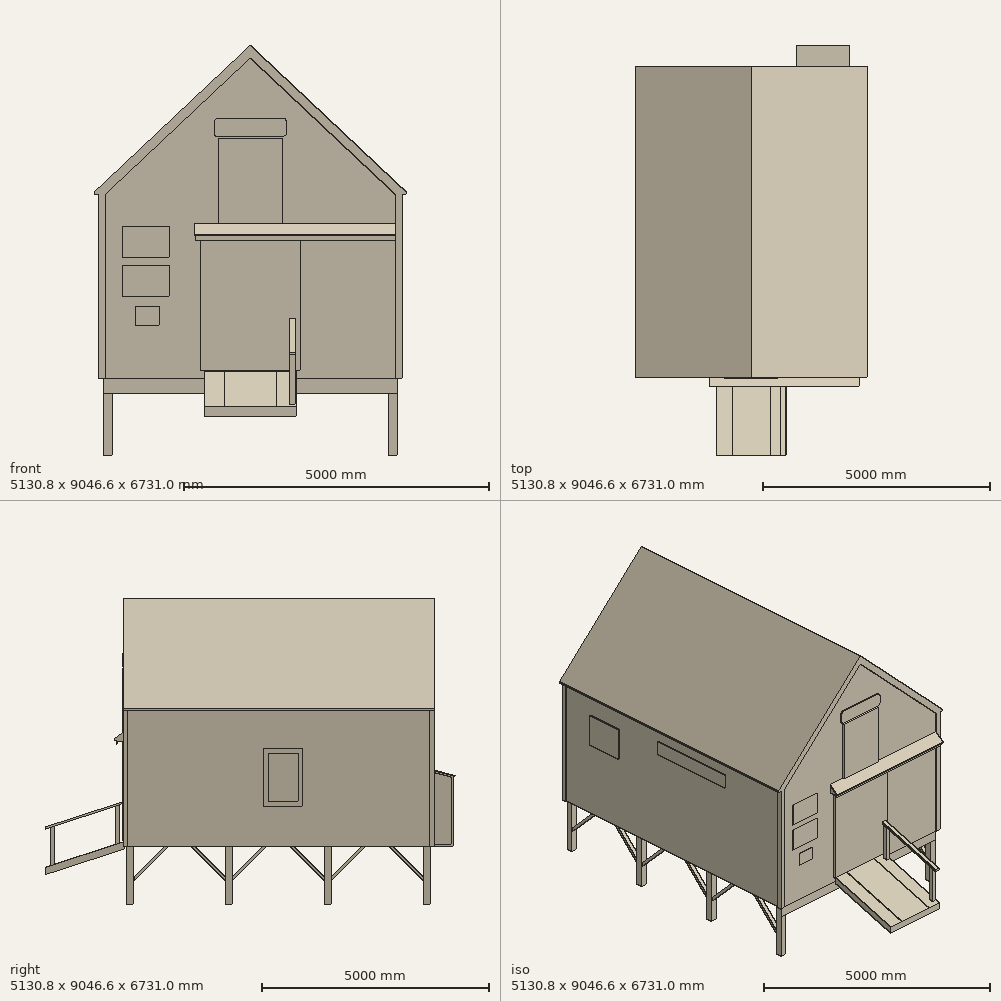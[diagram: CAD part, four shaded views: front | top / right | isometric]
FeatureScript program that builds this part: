
annotation { "Feature Type Name" : "Feature", "Feature Type Description" : "" }
export const myFeature = defineFeature(function(context is Context, id is Id, definition is map)
    precondition{}
    {
        {
            var Q0;
            Q0=qCreatedBy(makeId("Front.planeOp"),FACE);
            var sketch = newSketch(context, id + "F0", { "sketchPlane" : qUnion([Q0])});
            skLineSegment(sketch, "E0", {"start": v(0, 0) * mm, "end": v(0, 3048) * mm});
            skLineSegment(sketch, "E1", {"start": v(0, 3048) * mm, "end": v(2565.4, 5461) * mm});
            skLineSegment(sketch, "E2", {"start": v(2565.4, 5461) * mm, "end": v(5130.8, 3048) * mm});
            skLineSegment(sketch, "E3", {"start": v(5130.8, 3048) * mm, "end": v(5130.8, 0) * mm});
            skLineSegment(sketch, "E4", {"start": v(5130.8, 0) * mm, "end": v(0, 0) * mm});
            skLineSegment(sketch, "E5", {"start": v(2565.4, 5461) * mm, "end": v(2565.4, 0) * mm, "construction": true});
            skSolve(sketch);
        }
        {
            var Q0;
            Q0 = qSketchRegion(id + "F0", true);
            extrude(context, id + "F1", {"entities" : qUnion([Q0]), "oppositeDirection" : true, "depth" : 6858 * mm});
        }
        {
            var Q0;
            Q0=makeQuery(id+"F1.opExtrude","CAP_FACE",FACE,{"disambiguationData":[OSD([sQuery(id+"F0.wireOp",EDGE,"E0"),sQuery(id+"F0.wireOp",EDGE,"E1"),sQuery(id+"F0.wireOp",EDGE,"E2"),sQuery(id+"F0.wireOp",EDGE,"E3"),sQuery(id+"F0.wireOp",EDGE,"E4")])],"isStart":true});
            var sketch = newSketch(context, id + "F2", { "sketchPlane" : qUnion([Q0])});
            skLineSegment(sketch, "E6.bottom", {"start": v(0, 0) * mm, "end": v(76.2, 0) * mm});
            skLineSegment(sketch, "E6.top", {"start": v(0, 3009.9) * mm, "end": v(76.2, 3009.9) * mm});
            skLineSegment(sketch, "E6.left", {"start": v(0, 0) * mm, "end": v(0, 3009.9) * mm});
            skLineSegment(sketch, "E6.right", {"start": v(76.2, 0) * mm, "end": v(76.2, 3009.9) * mm});
            skLineSegment(sketch, "E7.bottom", {"start": v(5130.8, 0) * mm, "end": v(5054.6, 0) * mm});
            skLineSegment(sketch, "E7.top", {"start": v(5130.8, 3009.9) * mm, "end": v(5054.6, 3009.9) * mm});
            skLineSegment(sketch, "E7.left", {"start": v(5130.8, 0) * mm, "end": v(5130.8, 3009.9) * mm});
            skLineSegment(sketch, "E7.right", {"start": v(5054.6, 0) * mm, "end": v(5054.6, 3009.9) * mm});
            skSolve(sketch);
        }
        {
            var Q0;
            Q0 = qSketchRegion(id + "F2", true);
            extrude(context, id + "F3", {"entities" : qUnion([Q0]), "operationType" : NewBodyOperationType.REMOVE, "endBound" : BoundingType.THROUGH_ALL, "oppositeDirection" : true, "depth" : 25.4 * mm});
        }
        {
            var Q0;
            Q0=makeQuery(id+"F1.opExtrude","CAP_FACE",FACE,{"disambiguationData":[OSD([sQuery(id+"F0.wireOp",EDGE,"E0"),sQuery(id+"F0.wireOp",EDGE,"E1"),sQuery(id+"F0.wireOp",EDGE,"E2"),sQuery(id+"F0.wireOp",EDGE,"E3"),sQuery(id+"F0.wireOp",EDGE,"E4")])],"isStart":true});
            var sketch = newSketch(context, id + "F4", { "sketchPlane" : qUnion([Q0])});
            skLineSegment(sketch, "E8", {"start": v(177.8, 0) * mm, "end": v(177.8, 3006.02) * mm});
            skLineSegment(sketch, "E9", {"start": v(177.8, 3006.02) * mm, "end": v(2565.4, 5251.78) * mm});
            skLineSegment(sketch, "E10", {"start": v(2565.4, 5251.78) * mm, "end": v(4953, 3006.02) * mm});
            skLineSegment(sketch, "E11", {"start": v(4953, 3006.02) * mm, "end": v(4953, 0) * mm});
            skSolve(sketch);
        }
        {
            var Q0;
            {var subQ1=sQuery(id+"F4.wireOp",EDGE,"E8");Q0=makeQuery(id+"F4.imprint","IMPRINT",FACE,{"disambiguationData":[TD([[makeQuery(id+"F4.imprint","IMPRINT",EDGE,{"derivedFrom":subQ1}),-1.0]])]});}
            extrude(context, id + "F5", {"entities" : qUnion([Q0]), "operationType" : NewBodyOperationType.REMOVE, "oppositeDirection" : true, "depth" : 25.4 * mm});
        }
        {
            var Q0;
            Q0=makeQuery(id+"F1.opExtrude","CAP_FACE",FACE,{"disambiguationData":[OSD([sQuery(id+"F0.wireOp",EDGE,"E0"),sQuery(id+"F0.wireOp",EDGE,"E1"),sQuery(id+"F0.wireOp",EDGE,"E2"),sQuery(id+"F0.wireOp",EDGE,"E3"),sQuery(id+"F0.wireOp",EDGE,"E4")])],"isStart":false});
            var sketch = newSketch(context, id + "F6", { "sketchPlane" : qUnion([Q0])});
            skLineSegment(sketch, "E12.0.0", {"start": v(-4953, 0) * mm, "end": v(-4953, 3006.02) * mm});
            skLineSegment(sketch, "E12.0.1", {"start": v(-4953, 3006.02) * mm, "end": v(-2565.4, 5251.78) * mm});
            skLineSegment(sketch, "E12.0.2", {"start": v(-2565.4, 5251.78) * mm, "end": v(-177.8, 3006.02) * mm});
            skLineSegment(sketch, "E12.0.3", {"start": v(-177.8, 3006.02) * mm, "end": v(-177.8, 0) * mm});
            skLineSegment(sketch, "E12.0.4", {"start": v(-177.8, 0) * mm, "end": v(-4953, 0) * mm});
            skSolve(sketch);
        }
        {
            var Q0;
            Q0 = qSketchRegion(id + "F6", true);
            extrude(context, id + "F7", {"entities" : qUnion([Q0]), "operationType" : NewBodyOperationType.REMOVE, "oppositeDirection" : true, "depth" : 25.4 * mm});
        }
        {
            var Q0;
            Q0=makeQuery(id+"F3.boolean.opBoolean","COPY",FACE,{"derivedFrom":makeQuery(id+"F3.opExtrude","SWEPT_FACE",FACE,{"disambiguationData":[OSD([sQuery(id+"F2.wireOp",EDGE,"E6.right")])]})});
            var sketch = newSketch(context, id + "F8", { "sketchPlane" : qUnion([Q0])});
            skLineSegment(sketch, "E13.bottom", {"start": v(-6858, 0) * mm, "end": v(-6756.4, 0) * mm});
            skLineSegment(sketch, "E13.top", {"start": v(-6858, 3009.9) * mm, "end": v(-6756.4, 3009.9) * mm});
            skLineSegment(sketch, "E13.left", {"start": v(-6858, 0) * mm, "end": v(-6858, 3009.9) * mm});
            skLineSegment(sketch, "E13.right", {"start": v(-6756.4, 0) * mm, "end": v(-6756.4, 3009.9) * mm});
            skLineSegment(sketch, "E14.bottom", {"start": v(0, 0) * mm, "end": v(-101.6, 0) * mm});
            skLineSegment(sketch, "E14.top", {"start": v(0, 3009.9) * mm, "end": v(-101.6, 3009.9) * mm});
            skLineSegment(sketch, "E14.left", {"start": v(0, 0) * mm, "end": v(0, 3009.9) * mm});
            skLineSegment(sketch, "E14.right", {"start": v(-101.6, 0) * mm, "end": v(-101.6, 3009.9) * mm});
            skSolve(sketch);
        }
        {
            var Q0;
            {var subQ0=sQuery(id+"F8.wireOp",EDGE,"E13.right");Q0=makeQuery(id+"F8.imprint","IMPRINT",FACE,{"disambiguationData":[TD([[makeQuery(id+"F8.imprint","IMPRINT",EDGE,{"derivedFrom":subQ0}),-1.0]])]});}
            extrude(context, id + "F9", {"entities" : qUnion([Q0]), "operationType" : NewBodyOperationType.REMOVE, "oppositeDirection" : true, "depth" : 25.4 * mm});
        }
        {
            var Q0;
            Q0=makeQuery(id+"F3.boolean.opBoolean","COPY",FACE,{"derivedFrom":makeQuery(id+"F3.opExtrude","SWEPT_FACE",FACE,{"disambiguationData":[OSD([sQuery(id+"F2.wireOp",EDGE,"E7.right")])]})});
            var sketch = newSketch(context, id + "F10", { "sketchPlane" : qUnion([Q0])});
            skLineSegment(sketch, "E15.0.0", {"start": v(6756.4, 0) * mm, "end": v(101.6, 0) * mm});
            skLineSegment(sketch, "E15.0.1", {"start": v(101.6, 0) * mm, "end": v(101.6, 3009.9) * mm});
            skLineSegment(sketch, "E15.0.2", {"start": v(101.6, 3009.9) * mm, "end": v(6756.4, 3009.9) * mm});
            skLineSegment(sketch, "E15.0.3", {"start": v(6756.4, 3009.9) * mm, "end": v(6756.4, 0) * mm});
            skSolve(sketch);
        }
        {
            var Q0;
            Q0 = qSketchRegion(id + "F10", true);
            extrude(context, id + "F11", {"entities" : qUnion([Q0]), "operationType" : NewBodyOperationType.REMOVE, "oppositeDirection" : true, "depth" : 25.4 * mm});
        }
        {
            var Q0;
            Q0=makeQuery(id+"F1.opExtrude","SWEPT_FACE",FACE,{"disambiguationData":[OSD([sQuery(id+"F0.wireOp",EDGE,"E4")])]});
            var sketch = newSketch(context, id + "F12", { "sketchPlane" : qUnion([Q0])});
            skLineSegment(sketch, "E16.bottom", {"start": v(152.4, -76.2) * mm, "end": v(304.8, -76.2) * mm});
            skLineSegment(sketch, "E16.top", {"start": v(152.4, -228.6) * mm, "end": v(304.8, -228.6) * mm});
            skLineSegment(sketch, "E16.left", {"start": v(152.4, -76.2) * mm, "end": v(152.4, -228.6) * mm});
            skLineSegment(sketch, "E16.right", {"start": v(304.8, -76.2) * mm, "end": v(304.8, -228.6) * mm});
            skLineSegment(sketch, "E17.bottom", {"start": v(152.4, -2260.6) * mm, "end": v(304.8, -2260.6) * mm});
            skLineSegment(sketch, "E17.top", {"start": v(152.4, -2413) * mm, "end": v(304.8, -2413) * mm});
            skLineSegment(sketch, "E17.left", {"start": v(152.4, -2260.6) * mm, "end": v(152.4, -2413) * mm});
            skLineSegment(sketch, "E17.right", {"start": v(304.8, -2260.6) * mm, "end": v(304.8, -2413) * mm});
            skLineSegment(sketch, "E18.bottom", {"start": v(152.4, -4445) * mm, "end": v(304.8, -4445) * mm});
            skLineSegment(sketch, "E18.top", {"start": v(152.4, -4597.4) * mm, "end": v(304.8, -4597.4) * mm});
            skLineSegment(sketch, "E18.left", {"start": v(152.4, -4445) * mm, "end": v(152.4, -4597.4) * mm});
            skLineSegment(sketch, "E18.right", {"start": v(304.8, -4445) * mm, "end": v(304.8, -4597.4) * mm});
            skLineSegment(sketch, "E19.bottom", {"start": v(152.4, -6629.4) * mm, "end": v(304.8, -6629.4) * mm});
            skLineSegment(sketch, "E19.top", {"start": v(152.4, -6781.8) * mm, "end": v(304.8, -6781.8) * mm});
            skLineSegment(sketch, "E19.left", {"start": v(152.4, -6629.4) * mm, "end": v(152.4, -6781.8) * mm});
            skLineSegment(sketch, "E19.right", {"start": v(304.8, -6629.4) * mm, "end": v(304.8, -6781.8) * mm});
            skLineSegment(sketch, "E20.bottom", {"start": v(4826, -6629.4) * mm, "end": v(4978.4, -6629.4) * mm});
            skLineSegment(sketch, "E20.top", {"start": v(4826, -6781.8) * mm, "end": v(4978.4, -6781.8) * mm});
            skLineSegment(sketch, "E20.left", {"start": v(4826, -6629.4) * mm, "end": v(4826, -6781.8) * mm});
            skLineSegment(sketch, "E20.right", {"start": v(4978.4, -6629.4) * mm, "end": v(4978.4, -6781.8) * mm});
            skLineSegment(sketch, "E21.bottom", {"start": v(4826, -4445) * mm, "end": v(4978.4, -4445) * mm});
            skLineSegment(sketch, "E21.top", {"start": v(4826, -4597.4) * mm, "end": v(4978.4, -4597.4) * mm});
            skLineSegment(sketch, "E21.left", {"start": v(4826, -4445) * mm, "end": v(4826, -4597.4) * mm});
            skLineSegment(sketch, "E21.right", {"start": v(4978.4, -4445) * mm, "end": v(4978.4, -4597.4) * mm});
            skLineSegment(sketch, "E22.bottom", {"start": v(4826, -2260.6) * mm, "end": v(4978.4, -2260.6) * mm});
            skLineSegment(sketch, "E22.top", {"start": v(4826, -2413) * mm, "end": v(4978.4, -2413) * mm});
            skLineSegment(sketch, "E22.left", {"start": v(4826, -2260.6) * mm, "end": v(4826, -2413) * mm});
            skLineSegment(sketch, "E22.right", {"start": v(4978.4, -2260.6) * mm, "end": v(4978.4, -2413) * mm});
            skLineSegment(sketch, "E23.bottom", {"start": v(4826, -76.2) * mm, "end": v(4978.4, -76.2) * mm});
            skLineSegment(sketch, "E23.top", {"start": v(4826, -228.6) * mm, "end": v(4978.4, -228.6) * mm});
            skLineSegment(sketch, "E23.left", {"start": v(4826, -76.2) * mm, "end": v(4826, -228.6) * mm});
            skLineSegment(sketch, "E23.right", {"start": v(4978.4, -76.2) * mm, "end": v(4978.4, -228.6) * mm});
            skLineSegment(sketch, "E24", {"start": v(304.8, -228.6) * mm, "end": v(304.8, -2260.6) * mm, "construction": true});
            skLineSegment(sketch, "E25", {"start": v(304.8, -2413) * mm, "end": v(304.8, -4445) * mm, "construction": true});
            skLineSegment(sketch, "E26", {"start": v(304.8, -6629.4) * mm, "end": v(304.8, -4597.4) * mm, "construction": true});
            skSolve(sketch);
        }
        {
            var Q0;
            Q0 = qSketchRegion(id + "F12", true);
            extrude(context, id + "F13", {"entities" : qUnion([Q0]), "operationType" : NewBodyOperationType.ADD, "depth" : 1270 * mm});
        }
        {
            var Q0;
            Q0=makeQuery(id+"F13.opExtrude","SWEPT_FACE",FACE,{"disambiguationData":[OSD([sQuery(id+"F12.wireOp",EDGE,"E22.right")])]});
            cPlane(context, id + "F14", {"entities" : qUnion([Q0]), "cplaneType" : CPlaneType.OFFSET, "offset" : 25.4 * mm, "oppositeDirection" : true, "width" : 152.4 * mm, "height" : 152.4 * mm});
        }
        {
            var Q0;
            Q0=qCreatedBy(id+"F14.planeOp",FACE);
            var sketch = newSketch(context, id + "F15", { "sketchPlane" : qUnion([Q0])});
            skLineSegment(sketch, "E27", {"start": v(1588.4, 0) * mm, "end": v(2260.6, -672.2) * mm});
            skLineSegment(sketch, "E28", {"start": v(2260.6, -672.2) * mm, "end": v(2260.6, -762) * mm});
            skLineSegment(sketch, "E29", {"start": v(2260.6, -762) * mm, "end": v(1498.6, 0) * mm});
            skLineSegment(sketch, "E30", {"start": v(1498.6, 0) * mm, "end": v(1588.4, 0) * mm});
            skLineSegment(sketch, "E31", {"start": v(2413, -672.2) * mm, "end": v(3085.2, 0) * mm});
            skLineSegment(sketch, "E32", {"start": v(3085.2, 0) * mm, "end": v(3175, 0) * mm});
            skLineSegment(sketch, "E33", {"start": v(3175, 0) * mm, "end": v(2413, -762) * mm});
            skLineSegment(sketch, "E34", {"start": v(2413, -762) * mm, "end": v(2413, -672.2) * mm});
            skLineSegment(sketch, "E35.1.0.0", {"start": v(4597.4, -672.2) * mm, "end": v(5269.6, 0) * mm});
            skLineSegment(sketch, "E35.1.0.1", {"start": v(4445, -762) * mm, "end": v(3683, 0) * mm});
            skLineSegment(sketch, "E35.1.0.2", {"start": v(5359.4, 0) * mm, "end": v(4597.4, -762) * mm});
            skLineSegment(sketch, "E35.1.0.3", {"start": v(3772.8, 0) * mm, "end": v(4445, -672.2) * mm});
            skLineSegment(sketch, "E35.1.0.4", {"start": v(4445, -672.2) * mm, "end": v(4445, -762) * mm});
            skLineSegment(sketch, "E35.1.0.5", {"start": v(5269.6, 0) * mm, "end": v(5359.4, 0) * mm});
            skLineSegment(sketch, "E35.1.0.6", {"start": v(3683, 0) * mm, "end": v(3772.8, 0) * mm});
            skLineSegment(sketch, "E35.1.0.7", {"start": v(4597.4, -762) * mm, "end": v(4597.4, -672.2) * mm});
            skLineSegment(sketch, "E35.2.0.1", {"start": v(6629.4, -762) * mm, "end": v(5867.4, 0) * mm});
            skLineSegment(sketch, "E35.2.0.3", {"start": v(5957.2, 0) * mm, "end": v(6629.4, -672.2) * mm});
            skLineSegment(sketch, "E35.2.0.4", {"start": v(6629.4, -672.2) * mm, "end": v(6629.4, -762) * mm});
            skLineSegment(sketch, "E35.2.0.6", {"start": v(5867.4, 0) * mm, "end": v(5957.2, 0) * mm});
            skLineSegment(sketch, "E35.direction1", {"start": v(2260.6, -762) * mm, "end": v(4445, -762) * mm, "construction": true});
            skLineSegment(sketch, "E36.1.0.2", {"start": v(254, -672.2) * mm, "end": v(926.2, 0) * mm});
            skLineSegment(sketch, "E36.1.0.3", {"start": v(1016, 0) * mm, "end": v(254, -762) * mm});
            skLineSegment(sketch, "E36.1.0.5", {"start": v(926.2, 0) * mm, "end": v(1016, 0) * mm});
            skLineSegment(sketch, "E36.1.0.6", {"start": v(254, -762) * mm, "end": v(254, -672.2) * mm});
            skLineSegment(sketch, "E36.direction1", {"start": v(2260.6, -762) * mm, "end": v(254, -762) * mm, "construction": true});
            skSolve(sketch);
        }
        {
            var Q0;
            Q0 = qSketchRegion(id + "F15", true);
            extrude(context, id + "F16", {"entities" : qUnion([Q0]), "operationType" : NewBodyOperationType.ADD, "oppositeDirection" : true, "depth" : 101.6 * mm});
        }
        {
            var Q0;
            Q0=makeQuery(id+"F1.opExtrude","SWEPT_FACE",FACE,{"disambiguationData":[OSD([sQuery(id+"F0.wireOp",EDGE,"E4")])]});
            var sketch = newSketch(context, id + "F17", { "sketchPlane" : qUnion([Q0])});
            skLineSegment(sketch, "E37.bottom", {"start": v(228.6, -76.2) * mm, "end": v(4927.6, -76.2) * mm});
            skLineSegment(sketch, "E37.top", {"start": v(228.6, -152.4) * mm, "end": v(4927.6, -152.4) * mm});
            skLineSegment(sketch, "E37.left", {"start": v(228.6, -76.2) * mm, "end": v(228.6, -152.4) * mm});
            skLineSegment(sketch, "E37.right", {"start": v(4927.6, -76.2) * mm, "end": v(4927.6, -152.4) * mm});
            skSolve(sketch);
        }
        {
            var Q0;
            Q0 = qSketchRegion(id + "F17", true);
            extrude(context, id + "F18", {"entities" : qUnion([Q0]), "operationType" : NewBodyOperationType.ADD, "depth" : 254 * mm});
        }
        {
            var Q0;
            Q0=makeQuery(id+"F13.opExtrude","SWEPT_FACE",FACE,{"disambiguationData":[OSD([sQuery(id+"F12.wireOp",EDGE,"E17.left")])]});
            cPlane(context, id + "F19", {"entities" : qUnion([Q0]), "cplaneType" : CPlaneType.OFFSET, "offset" : 25.4 * mm, "oppositeDirection" : true, "width" : 152.4 * mm, "height" : 152.4 * mm});
        }
        {
            var Q0;
            Q0=qCreatedBy(id+"F19.planeOp",FACE);
            var sketch = newSketch(context, id + "F20", { "sketchPlane" : qUnion([Q0])});
            skLineSegment(sketch, "E38.0.0", {"start": v(-1016, 0) * mm, "end": v(-216.67, -799.33) * mm});
            skLineSegment(sketch, "E38.0.1", {"start": v(-216.67, -799.33) * mm, "end": v(-228.85, -697.35) * mm});
            skLineSegment(sketch, "E38.0.2", {"start": v(-228.85, -697.35) * mm, "end": v(-926.2, 0) * mm});
            skLineSegment(sketch, "E38.0.3", {"start": v(-926.2, 0) * mm, "end": v(-1016, 0) * mm});
            skLineSegment(sketch, "E38.1.0", {"start": v(-1498.6, 0) * mm, "end": v(-1588.4, 0) * mm});
            skLineSegment(sketch, "E38.1.1", {"start": v(-1588.4, 0) * mm, "end": v(-2260.6, -672.2) * mm});
            skLineSegment(sketch, "E38.1.2", {"start": v(-2260.6, -672.2) * mm, "end": v(-2260.6, -762) * mm});
            skLineSegment(sketch, "E38.1.3", {"start": v(-2260.6, -762) * mm, "end": v(-1498.6, 0) * mm});
            skLineSegment(sketch, "E38.2.0", {"start": v(-2413, -762) * mm, "end": v(-2413, -672.2) * mm});
            skLineSegment(sketch, "E38.2.1", {"start": v(-2413, -672.2) * mm, "end": v(-3085.2, 0) * mm});
            skLineSegment(sketch, "E38.2.2", {"start": v(-3085.2, 0) * mm, "end": v(-3175, 0) * mm});
            skLineSegment(sketch, "E38.2.3", {"start": v(-3175, 0) * mm, "end": v(-2413, -762) * mm});
            skLineSegment(sketch, "E38.3.0", {"start": v(-4451.44, -678.64) * mm, "end": v(-4448.14, -765.14) * mm});
            skLineSegment(sketch, "E38.3.1", {"start": v(-4448.14, -765.14) * mm, "end": v(-3683, 0) * mm});
            skLineSegment(sketch, "E38.3.2", {"start": v(-3683, 0) * mm, "end": v(-3772.8, 0) * mm});
            skLineSegment(sketch, "E38.3.3", {"start": v(-3772.8, 0) * mm, "end": v(-4451.44, -678.64) * mm});
            skLineSegment(sketch, "E38.4.0", {"start": v(-5359.4, 0) * mm, "end": v(-4597.4, -762) * mm});
            skLineSegment(sketch, "E38.4.1", {"start": v(-4597.4, -762) * mm, "end": v(-4597.4, -672.2) * mm});
            skLineSegment(sketch, "E38.4.2", {"start": v(-4597.4, -672.2) * mm, "end": v(-5269.6, 0) * mm});
            skLineSegment(sketch, "E38.4.3", {"start": v(-5269.6, 0) * mm, "end": v(-5359.4, 0) * mm});
            skLineSegment(sketch, "E38.5.0", {"start": v(-6628.48, -671.28) * mm, "end": v(-6634.78, -767.38) * mm});
            skLineSegment(sketch, "E38.5.1", {"start": v(-6634.78, -767.38) * mm, "end": v(-5867.4, 0) * mm});
            skLineSegment(sketch, "E38.5.2", {"start": v(-5867.4, 0) * mm, "end": v(-5957.2, 0) * mm});
            skLineSegment(sketch, "E38.5.3", {"start": v(-5957.2, 0) * mm, "end": v(-6628.48, -671.28) * mm});
            skSolve(sketch);
        }
        {
            var Q0;
            Q0 = qSketchRegion(id + "F20", true);
            extrude(context, id + "F21", {"entities" : qUnion([Q0]), "operationType" : NewBodyOperationType.ADD, "oppositeDirection" : true, "depth" : 101.6 * mm});
        }
        {
            var Q0;
            Q0=makeQuery(id+"F5.boolean.opBoolean","COPY",FACE,{"derivedFrom":makeQuery(id+"F5.opExtrude","CAP_FACE",FACE,{"disambiguationData":[OSD([sQuery(id+"F0.wireOp",EDGE,"E4"),sQuery(id+"F4.wireOp",EDGE,"E8"),sQuery(id+"F4.wireOp",EDGE,"E9"),sQuery(id+"F4.wireOp",EDGE,"E10"),sQuery(id+"F4.wireOp",EDGE,"E11")])],"isStart":false})});
            var sketch = newSketch(context, id + "F22", { "sketchPlane" : qUnion([Q0])});
            skLineSegment(sketch, "E39.bottom", {"start": v(1739.9, 2286) * mm, "end": v(3390.9, 2286) * mm});
            skLineSegment(sketch, "E39.top", {"start": v(1739.9, 127) * mm, "end": v(3390.9, 127) * mm});
            skLineSegment(sketch, "E39.left", {"start": v(1739.9, 2286) * mm, "end": v(1739.9, 127) * mm});
            skLineSegment(sketch, "E39.right", {"start": v(3390.9, 2286) * mm, "end": v(3390.9, 127) * mm});
            skLineSegment(sketch, "E40", {"start": v(2565.4, 5251.78) * mm, "end": v(2565.4, 2286) * mm, "construction": true});
            skLineSegment(sketch, "E41.bottom", {"start": v(2032, 3937) * mm, "end": v(3098.8, 3937) * mm});
            skLineSegment(sketch, "E41.top", {"start": v(2032, 2540) * mm, "end": v(3098.8, 2540) * mm});
            skLineSegment(sketch, "E41.left", {"start": v(2032, 3937) * mm, "end": v(2032, 2540) * mm});
            skLineSegment(sketch, "E41.right", {"start": v(3098.8, 3937) * mm, "end": v(3098.8, 2540) * mm});
            skSolve(sketch);
        }
        {
            var Q0;
            Q0 = qSketchRegion(id + "F22", true);
            extrude(context, id + "F23", {"entities" : qUnion([Q0]), "operationType" : NewBodyOperationType.ADD, "depth" : 50.8 * mm});
        }
        {
            var Q0;
            Q0=makeQuery(id+"F23.opExtrude","SWEPT_FACE",FACE,{"disambiguationData":[OSD([sQuery(id+"F22.wireOp",EDGE,"E39.left")])]});
            cPlane(context, id + "F24", {"entities" : qUnion([Q0]), "cplaneType" : CPlaneType.OFFSET, "offset" : 101.6 * mm, "width" : 152.4 * mm, "height" : 152.4 * mm});
        }
        {
            var Q0;
            Q0=qCreatedBy(id+"F24.planeOp",FACE);
            var sketch = newSketch(context, id + "F25", { "sketchPlane" : qUnion([Q0])});
            skLineSegment(sketch, "E42", {"start": v(-25.4, 2540) * mm, "end": v(203.2, 2362.2) * mm});
            skLineSegment(sketch, "E43", {"start": v(203.2, 2362.2) * mm, "end": v(203.2, 2336.8) * mm});
            skLineSegment(sketch, "E44", {"start": v(203.2, 2336.8) * mm, "end": v(152.4, 2336.8) * mm});
            skLineSegment(sketch, "E45", {"start": v(152.4, 2336.8) * mm, "end": v(152.4, 2260.6) * mm});
            skLineSegment(sketch, "E46", {"start": v(152.4, 2260.6) * mm, "end": v(127, 2260.6) * mm});
            skLineSegment(sketch, "E47", {"start": v(127, 2260.6) * mm, "end": v(127, 2311.4) * mm});
            skLineSegment(sketch, "E48", {"start": v(127, 2311.4) * mm, "end": v(-25.4, 2311.4) * mm});
            skLineSegment(sketch, "E49", {"start": v(-25.4, 2540) * mm, "end": v(-25.4, 2311.4) * mm});
            skSolve(sketch);
        }
        {
            var Q0;
            Q0 = qSketchRegion(id + "F25", true);
            var Q1;
            Q1=makeQuery(id+"F5.boolean.opBoolean","COPY",FACE,{"derivedFrom":makeQuery(id+"F5.opExtrude","SWEPT_FACE",FACE,{"disambiguationData":[OSD([sQuery(id+"F4.wireOp",EDGE,"E11")])]})});
            extrude(context, id + "F26", {"entities" : qUnion([Q0]), "operationType" : NewBodyOperationType.ADD, "endBound" : BoundingType.UP_TO_SURFACE, "oppositeDirection" : true, "endBoundEntityFace" : qUnion([Q1]), "depth" : 25.4 * mm});
        }
        {
            var Q0;
            Q0=makeQuery(id+"F26.opExtrude","CAP_FACE",FACE,{"disambiguationData":[OSD([sQuery(id+"F25.wireOp",EDGE,"E42"),sQuery(id+"F25.wireOp",EDGE,"E43"),sQuery(id+"F25.wireOp",EDGE,"E44"),sQuery(id+"F25.wireOp",EDGE,"E45"),sQuery(id+"F25.wireOp",EDGE,"E46"),sQuery(id+"F25.wireOp",EDGE,"E47"),sQuery(id+"F25.wireOp",EDGE,"E48"),sQuery(id+"F25.wireOp",EDGE,"E49")])],"isStart":true});
            var sketch = newSketch(context, id + "F27", { "sketchPlane" : qUnion([Q0])});
            skLineSegment(sketch, "E50", {"start": v(203.2, 2336.8) * mm, "end": v(-25.4, 2514.6) * mm});
            skSolve(sketch);
        }
        {
            var Q0;
            {var subQ0=sQuery(id+"F27.wireOp",EDGE,"E50");Q0=makeQuery(id+"F27.imprint","IMPRINT",FACE,{"disambiguationData":[TD([[makeQuery(id+"F27.imprint","IMPRINT",EDGE,{"derivedFrom":subQ0}),1.0]])]});}
            extrude(context, id + "F28", {"entities" : qUnion([Q0]), "operationType" : NewBodyOperationType.REMOVE, "oppositeDirection" : true, "depth" : 25.4 * mm});
        }
        {
            var Q0;
            Q0=makeQuery(id+"F23.opExtrude","CAP_EDGE",EDGE,{"disambiguationData":[OSD([sQuery(id+"F22.wireOp",EDGE,"E39.top")])],"isStart":false});
            cPoint(context, id + "F29", {"entities" : qUnion([Q0]), "parameter" : 0.5});
        }
        {
            var Q0;
            Q0=makeQuery(id+"F23.opExtrude","SWEPT_FACE",FACE,{"disambiguationData":[OSD([sQuery(id+"F22.wireOp",EDGE,"E39.left")])]});
            var Q1;
            Q1 = qCreatedBy(id + "F29" ,VERTEX);
            cPlane(context, id + "F30", {"entities" : qUnion([Q0, Q1]), "cplaneType" : CPlaneType.PLANE_POINT, "offset" : 25.4 * mm, "width" : 152.4 * mm, "height" : 152.4 * mm});
        }
        {
            var Q0;
            Q0=qCreatedBy(id+"F30.planeOp",FACE);
            var sketch = newSketch(context, id + "F31", { "sketchPlane" : qUnion([Q0])});
            skLineSegment(sketch, "E51", {"start": v(-25.4, 101.6) * mm, "end": v(1713.9, -463.53) * mm});
            skLineSegment(sketch, "E52", {"start": v(1713.9, -463.53) * mm, "end": v(1713.9, -623.77) * mm});
            skLineSegment(sketch, "E53", {"start": v(1713.9, -623.77) * mm, "end": v(-25.4, -58.64) * mm});
            skLineSegment(sketch, "E54", {"start": v(-25.4, 101.6) * mm, "end": v(-25.4, -58.64) * mm});
            skSolve(sketch);
        }
        {
            var Q0;
            Q0 = qSketchRegion(id + "F31", true);
            extrude(context, id + "F32", {"entities" : qUnion([Q0]), "operationType" : NewBodyOperationType.ADD, "endBound" : BoundingType.SYMMETRIC, "depth" : 1524 * mm});
        }
        {
            var Q0;
            Q0=makeQuery(id+"F1.opExtrude","SWEPT_FACE",FACE,{"disambiguationData":[OSD([sQuery(id+"F0.wireOp",EDGE,"E4")])]});
            var sketch = newSketch(context, id + "F33", { "sketchPlane" : qUnion([Q0])});
            skLineSegment(sketch, "E55.bottom", {"start": v(3213.1, 1523.4) * mm, "end": v(3302, 1523.4) * mm});
            skLineSegment(sketch, "E55.top", {"start": v(3213.1, 1612.3) * mm, "end": v(3302, 1612.3) * mm});
            skLineSegment(sketch, "E55.left", {"start": v(3213.1, 1523.4) * mm, "end": v(3213.1, 1612.3) * mm});
            skLineSegment(sketch, "E55.right", {"start": v(3302, 1523.4) * mm, "end": v(3302, 1612.3) * mm});
            skLineSegment(sketch, "E56.bottom", {"start": v(3213.1, 76.2) * mm, "end": v(3302, 76.2) * mm});
            skLineSegment(sketch, "E56.top", {"start": v(3213.1, 165.1) * mm, "end": v(3302, 165.1) * mm});
            skLineSegment(sketch, "E56.left", {"start": v(3213.1, 76.2) * mm, "end": v(3213.1, 165.1) * mm});
            skLineSegment(sketch, "E56.right", {"start": v(3302, 76.2) * mm, "end": v(3302, 165.1) * mm});
            skSolve(sketch);
        }
        {
            var Q0;
            Q0 = qSketchRegion(id + "F33", true);
            var Q1;
            Q1=makeQuery(id+"F32.opExtrude","SWEPT_FACE",FACE,{"disambiguationData":[OSD([sQuery(id+"F31.wireOp",EDGE,"E53")])]});
            extrude(context, id + "F34", {"entities" : qUnion([Q0]), "operationType" : NewBodyOperationType.ADD, "endBound" : BoundingType.UP_TO_SURFACE, "endBoundEntityFace" : qUnion([Q1]), "depth" : 25.4 * mm, "hasSecondDirection" : true, "secondDirectionOppositeDirection" : true, "secondDirectionDepth" : 914.4 * mm});
        }
        {
            var Q0;
            Q0=makeQuery(id+"F34.opExtrude","SWEPT_FACE",FACE,{"disambiguationData":[OSD([sQuery(id+"F33.wireOp",EDGE,"E55.right")])]});
            var sketch = newSketch(context, id + "F35", { "sketchPlane" : qUnion([Q0])});
            skLineSegment(sketch, "E57", {"start": v(-76.2, 914.4) * mm, "end": v(-1612.3, 415.3) * mm});
            skLineSegment(sketch, "E58", {"start": v(-1612.3, 415.3) * mm, "end": v(-1612.3, 914.4) * mm});
            skLineSegment(sketch, "E59", {"start": v(-1612.3, 914.4) * mm, "end": v(-76.2, 914.4) * mm});
            skSolve(sketch);
        }
        {
            var Q0;
            Q0 = qSketchRegion(id + "F35", true);
            extrude(context, id + "F36", {"entities" : qUnion([Q0]), "operationType" : NewBodyOperationType.REMOVE, "oppositeDirection" : true, "depth" : 508 * mm});
        }
        {
            var Q0;
            Q0=makeQuery(id+"F34.opExtrude","SWEPT_FACE",FACE,{"disambiguationData":[OSD([sQuery(id+"F33.wireOp",EDGE,"E56.right")])]});
            var sketch = newSketch(context, id + "F37", { "sketchPlane" : qUnion([Q0])});
            skLineSegment(sketch, "E60", {"start": v(-42.27, 925.43) * mm, "end": v(-1713.9, 382.28) * mm});
            skLineSegment(sketch, "E61", {"start": v(-1713.9, 382.28) * mm, "end": v(-1713.9, 429.02) * mm});
            skLineSegment(sketch, "E62", {"start": v(-1713.9, 429.02) * mm, "end": v(-42.27, 972.16) * mm});
            skLineSegment(sketch, "E63", {"start": v(-42.27, 972.16) * mm, "end": v(-42.27, 925.43) * mm});
            skSolve(sketch);
        }
        {
            var Q0;
            Q0 = qSketchRegion(id + "F37", true);
            extrude(context, id + "F38", {"entities" : qUnion([Q0]), "operationType" : NewBodyOperationType.ADD, "depth" : 6.35 * mm, "hasSecondDirection" : true, "secondDirectionOppositeDirection" : true, "secondDirectionDepth" : 95.25 * mm});
        }
        {
            var Q0;
            Q0=makeQuery(id+"F32.opExtrude","SWEPT_FACE",FACE,{"disambiguationData":[OSD([sQuery(id+"F31.wireOp",EDGE,"E51")])]});
            var sketch = newSketch(context, id + "F39", { "sketchPlane" : qUnion([Q0])});
            skLineSegment(sketch, "E64.bottom", {"start": v(2146.66, 55.55) * mm, "end": v(2995.5, 55.55) * mm});
            skLineSegment(sketch, "E64.top", {"start": v(2146.66, -1773.25) * mm, "end": v(2995.5, -1773.25) * mm});
            skLineSegment(sketch, "E64.left", {"start": v(2146.66, 55.55) * mm, "end": v(2146.66, -1773.25) * mm});
            skLineSegment(sketch, "E64.right", {"start": v(2995.5, 55.55) * mm, "end": v(2995.5, -1773.25) * mm});
            skSolve(sketch);
        }
        {
            var Q0;
            Q0 = qSketchRegion(id + "F39", true);
            extrude(context, id + "F40", {"entities" : qUnion([Q0]), "operationType" : NewBodyOperationType.ADD, "depth" : 6.35 * mm});
        }
        {
            var Q0;
            Q0=makeQuery(id+"F28.boolean.opBoolean","MERGE",FACE,{"derivedFrom":[makeQuery(id+"F5.boolean.opBoolean","COPY",FACE,{"derivedFrom":makeQuery(id+"F5.opExtrude","CAP_FACE",FACE,{"disambiguationData":[OSD([sQuery(id+"F0.wireOp",EDGE,"E4"),sQuery(id+"F4.wireOp",EDGE,"E8"),sQuery(id+"F4.wireOp",EDGE,"E9"),sQuery(id+"F4.wireOp",EDGE,"E10"),sQuery(id+"F4.wireOp",EDGE,"E11")])],"isStart":false})}),makeQuery(id+"F28.opExtrude","SWEPT_FACE",FACE,{"disambiguationData":[OSD([sQuery(id+"F25.wireOp",EDGE,"E49")])]})]});
            var sketch = newSketch(context, id + "F41", { "sketchPlane" : qUnion([Q0])});
            skLineSegment(sketch, "E65.bottom", {"start": v(2019.89, 4267.2) * mm, "end": v(3121.97, 4267.2) * mm});
            skLineSegment(sketch, "E65.top", {"start": v(2007.07, 3962.4) * mm, "end": v(3113.43, 3962.4) * mm});
            skLineSegment(sketch, "E65.left", {"start": v(1968.5, 4221.72) * mm, "end": v(1968.5, 4006) * mm});
            skLineSegment(sketch, "E65.right", {"start": v(3162.3, 4221.72) * mm, "end": v(3162.3, 3999.6) * mm});
            skLineSegment(sketch, "E66", {"start": v(2019.89, 4267.2) * mm, "end": v(1968.5, 4221.72) * mm});
            skLineSegment(sketch, "E67", {"start": v(1968.5, 4006) * mm, "end": v(2007.07, 3962.4) * mm});
            skLineSegment(sketch, "E68", {"start": v(3113.43, 3962.4) * mm, "end": v(3162.3, 3999.6) * mm});
            skLineSegment(sketch, "E69", {"start": v(3121.97, 4267.2) * mm, "end": v(3162.3, 4221.72) * mm});
            skSolve(sketch);
        }
        {
            var Q0;
            Q0 = qSketchRegion(id + "F41", true);
            extrude(context, id + "F42", {"entities" : qUnion([Q0]), "operationType" : NewBodyOperationType.ADD, "depth" : 38.1 * mm});
        }
        {
            var Q0;
            Q0=makeQuery(id+"F28.boolean.opBoolean","MERGE",FACE,{"derivedFrom":[makeQuery(id+"F5.boolean.opBoolean","COPY",FACE,{"derivedFrom":makeQuery(id+"F5.opExtrude","CAP_FACE",FACE,{"disambiguationData":[OSD([sQuery(id+"F0.wireOp",EDGE,"E4"),sQuery(id+"F4.wireOp",EDGE,"E8"),sQuery(id+"F4.wireOp",EDGE,"E9"),sQuery(id+"F4.wireOp",EDGE,"E10"),sQuery(id+"F4.wireOp",EDGE,"E11")])],"isStart":false})}),makeQuery(id+"F28.opExtrude","SWEPT_FACE",FACE,{"disambiguationData":[OSD([sQuery(id+"F25.wireOp",EDGE,"E49")])]})]});
            var sketch = newSketch(context, id + "F43", { "sketchPlane" : qUnion([Q0])});
            skLineSegment(sketch, "E70.bottom", {"start": v(469.9, 2489.2) * mm, "end": v(1231.9, 2489.2) * mm});
            skLineSegment(sketch, "E70.top", {"start": v(469.9, 1981.2) * mm, "end": v(1231.9, 1981.2) * mm});
            skLineSegment(sketch, "E70.left", {"start": v(469.9, 2489.2) * mm, "end": v(469.9, 1981.2) * mm});
            skLineSegment(sketch, "E70.right", {"start": v(1231.9, 2489.2) * mm, "end": v(1231.9, 1981.2) * mm});
            skLineSegment(sketch, "E71.bottom", {"start": v(469.9, 1854.2) * mm, "end": v(1231.9, 1854.2) * mm});
            skLineSegment(sketch, "E71.top", {"start": v(469.9, 1346.2) * mm, "end": v(1231.9, 1346.2) * mm});
            skLineSegment(sketch, "E71.left", {"start": v(469.9, 1854.2) * mm, "end": v(469.9, 1346.2) * mm});
            skLineSegment(sketch, "E71.right", {"start": v(1231.9, 1854.2) * mm, "end": v(1231.9, 1346.2) * mm});
            skLineSegment(sketch, "E72.bottom", {"start": v(673.1, 1168.4) * mm, "end": v(1079.5, 1168.4) * mm});
            skLineSegment(sketch, "E72.top", {"start": v(673.1, 863.6) * mm, "end": v(1079.5, 863.6) * mm});
            skLineSegment(sketch, "E72.left", {"start": v(673.1, 1168.4) * mm, "end": v(673.1, 863.6) * mm});
            skLineSegment(sketch, "E72.right", {"start": v(1079.5, 1168.4) * mm, "end": v(1079.5, 863.6) * mm});
            skSolve(sketch);
        }
        {
            var Q0;
            Q0 = qSketchRegion(id + "F43", true);
            extrude(context, id + "F44", {"entities" : qUnion([Q0]), "operationType" : NewBodyOperationType.ADD, "depth" : 6.35 * mm});
        }
        {
            var Q0;
            Q0=makeQuery(id+"F11.boolean.opBoolean","COPY",FACE,{"derivedFrom":makeQuery(id+"F11.opExtrude","CAP_FACE",FACE,{"disambiguationData":[OSD([sQuery(id+"F10.wireOp",EDGE,"E15.0.0"),sQuery(id+"F10.wireOp",EDGE,"E15.0.1"),sQuery(id+"F10.wireOp",EDGE,"E15.0.2"),sQuery(id+"F10.wireOp",EDGE,"E15.0.3")])],"isStart":false})});
            var sketch = newSketch(context, id + "F45", { "sketchPlane" : qUnion([Q0])});
            skLineSegment(sketch, "E73.bottom", {"start": v(3098.8, 2159) * mm, "end": v(3962.4, 2159) * mm});
            skLineSegment(sketch, "E73.top", {"start": v(3098.8, 889) * mm, "end": v(3962.4, 889) * mm});
            skLineSegment(sketch, "E73.left", {"start": v(3098.8, 2159) * mm, "end": v(3098.8, 889) * mm});
            skLineSegment(sketch, "E73.right", {"start": v(3962.4, 2159) * mm, "end": v(3962.4, 889) * mm});
            skSolve(sketch);
        }
        {
            var Q0;
            Q0 = qSketchRegion(id + "F45", true);
            extrude(context, id + "F46", {"entities" : qUnion([Q0]), "operationType" : NewBodyOperationType.ADD, "depth" : 25.4 * mm});
        }
        {
            var Q0;
            Q0=makeQuery(id+"F46.opExtrude","CAP_FACE",FACE,{"disambiguationData":[OSD([sQuery(id+"F45.wireOp",EDGE,"E73.bottom"),sQuery(id+"F45.wireOp",EDGE,"E73.top"),sQuery(id+"F45.wireOp",EDGE,"E73.left"),sQuery(id+"F45.wireOp",EDGE,"E73.right")])],"isStart":false});
            var sketch = newSketch(context, id + "F47", { "sketchPlane" : qUnion([Q0])});
            skLineSegment(sketch, "E74.0", {"start": v(3200.4, 2057.4) * mm, "end": v(3200.4, 990.6) * mm});
            skLineSegment(sketch, "E74.1", {"start": v(3860.8, 2057.4) * mm, "end": v(3200.4, 2057.4) * mm});
            skLineSegment(sketch, "E74.2", {"start": v(3860.8, 990.6) * mm, "end": v(3860.8, 2057.4) * mm});
            skLineSegment(sketch, "E74.3", {"start": v(3200.4, 990.6) * mm, "end": v(3860.8, 990.6) * mm});
            skSolve(sketch);
        }
        {
            var Q0;
            Q0 = qSketchRegion(id + "F47", true);
            extrude(context, id + "F48", {"entities" : qUnion([Q0]), "operationType" : NewBodyOperationType.REMOVE, "oppositeDirection" : true, "depth" : 25.4 * mm});
        }
        {
            var Q0;
            Q0=makeQuery(id+"F7.boolean.opBoolean","COPY",FACE,{"derivedFrom":makeQuery(id+"F7.opExtrude","CAP_FACE",FACE,{"disambiguationData":[OSD([sQuery(id+"F6.wireOp",EDGE,"E12.0.0"),sQuery(id+"F6.wireOp",EDGE,"E12.0.1"),sQuery(id+"F6.wireOp",EDGE,"E12.0.2"),sQuery(id+"F6.wireOp",EDGE,"E12.0.3"),sQuery(id+"F6.wireOp",EDGE,"E12.0.4")])],"isStart":false})});
            var sketch = newSketch(context, id + "F49", { "sketchPlane" : qUnion([Q0])});
            skLineSegment(sketch, "E75.bottom", {"start": v(-2997.2, 4377.62) * mm, "end": v(-2133.6, 4377.62) * mm});
            skLineSegment(sketch, "E75.top", {"start": v(-2997.2, 2980.62) * mm, "end": v(-2133.6, 2980.62) * mm});
            skLineSegment(sketch, "E75.left", {"start": v(-2997.2, 4377.62) * mm, "end": v(-2997.2, 2980.62) * mm});
            skLineSegment(sketch, "E75.right", {"start": v(-2133.6, 4377.62) * mm, "end": v(-2133.6, 2980.62) * mm});
            skLineSegment(sketch, "E76", {"start": v(-2565.4, 5251.78) * mm, "end": v(-2565.4, 4377.62) * mm, "construction": true});
            skSolve(sketch);
        }
        {
            var Q0;
            Q0 = qSketchRegion(id + "F49", true);
            extrude(context, id + "F50", {"entities" : qUnion([Q0]), "operationType" : NewBodyOperationType.ADD, "depth" : 25.4 * mm});
        }
        {
            var Q0;
            Q0=makeQuery(id+"F50.opExtrude","CAP_FACE",FACE,{"disambiguationData":[OSD([sQuery(id+"F49.wireOp",EDGE,"E75.bottom"),sQuery(id+"F49.wireOp",EDGE,"E75.top"),sQuery(id+"F49.wireOp",EDGE,"E75.left"),sQuery(id+"F49.wireOp",EDGE,"E75.right")])],"isStart":false});
            var sketch = newSketch(context, id + "F51", { "sketchPlane" : qUnion([Q0])});
            skLineSegment(sketch, "E77.0", {"start": v(-2921, 4301.42) * mm, "end": v(-2921, 3056.82) * mm});
            skLineSegment(sketch, "E77.1", {"start": v(-2209.8, 4301.42) * mm, "end": v(-2921, 4301.42) * mm});
            skLineSegment(sketch, "E77.2", {"start": v(-2209.8, 3056.82) * mm, "end": v(-2209.8, 4301.42) * mm});
            skLineSegment(sketch, "E77.3", {"start": v(-2921, 3056.82) * mm, "end": v(-2209.8, 3056.82) * mm});
            skSolve(sketch);
        }
        {
            var Q0;
            Q0 = qSketchRegion(id + "F51", true);
            extrude(context, id + "F52", {"entities" : qUnion([Q0]), "operationType" : NewBodyOperationType.REMOVE, "oppositeDirection" : true, "depth" : 50.8 * mm});
        }
        {
            var Q0;
            Q0=makeQuery(id+"F11.boolean.opBoolean","COPY",FACE,{"derivedFrom":makeQuery(id+"F11.opExtrude","CAP_FACE",FACE,{"disambiguationData":[OSD([sQuery(id+"F10.wireOp",EDGE,"E15.0.0"),sQuery(id+"F10.wireOp",EDGE,"E15.0.1"),sQuery(id+"F10.wireOp",EDGE,"E15.0.2"),sQuery(id+"F10.wireOp",EDGE,"E15.0.3")])],"isStart":false})});
            cPlane(context, id + "F53", {"entities" : qUnion([Q0]), "cplaneType" : CPlaneType.OFFSET, "offset" : 889 * mm, "oppositeDirection" : true, "width" : 152.4 * mm, "height" : 152.4 * mm});
        }
        {
            var Q0;
            Q0=qCreatedBy(id+"F53.planeOp",FACE);
            var sketch = newSketch(context, id + "F54", { "sketchPlane" : qUnion([Q0])});
            skLineSegment(sketch, "E78", {"start": v(6832.6, 0) * mm, "end": v(6832.6, 1678.71) * mm});
            skLineSegment(sketch, "E79", {"start": v(6832.6, 1678.71) * mm, "end": v(7315.2, 1549.4) * mm});
            skLineSegment(sketch, "E80", {"start": v(7315.2, 1524) * mm, "end": v(7289.8, 1524) * mm});
            skLineSegment(sketch, "E81", {"start": v(7289.8, 1524) * mm, "end": v(7289.8, 0) * mm});
            skLineSegment(sketch, "E82", {"start": v(7315.2, 1549.4) * mm, "end": v(7315.2, 1524) * mm});
            skLineSegment(sketch, "E83", {"start": v(7289.8, 0) * mm, "end": v(6832.6, 0) * mm});
            skSolve(sketch);
        }
        {
            var Q0;
            Q0 = qSketchRegion(id + "F54", true);
            extrude(context, id + "F55", {"entities" : qUnion([Q0]), "operationType" : NewBodyOperationType.ADD, "endBound" : BoundingType.SYMMETRIC, "depth" : 1143 * mm});
        }
        {
            var Q0;
            Q0=makeQuery(id+"F55.opExtrude","SWEPT_FACE",FACE,{"disambiguationData":[OSD([sQuery(id+"F54.wireOp",EDGE,"E81")])]});
            var sketch = newSketch(context, id + "F56", { "sketchPlane" : qUnion([Q0])});
            skLineSegment(sketch, "E84.bottom", {"start": v(-4673.6, 0) * mm, "end": v(-3606.8, 0) * mm});
            skLineSegment(sketch, "E84.top", {"start": v(-4673.6, 1498.6) * mm, "end": v(-3606.8, 1498.6) * mm});
            skLineSegment(sketch, "E84.left", {"start": v(-4673.6, 0) * mm, "end": v(-4673.6, 1498.6) * mm});
            skLineSegment(sketch, "E84.right", {"start": v(-3606.8, 0) * mm, "end": v(-3606.8, 1498.6) * mm});
            skSolve(sketch);
        }
        {
            var Q0;
            Q0 = qSketchRegion(id + "F56", true);
            extrude(context, id + "F57", {"entities" : qUnion([Q0]), "operationType" : NewBodyOperationType.REMOVE, "oppositeDirection" : true, "depth" : 12.7 * mm});
        }
        {
            var Q0;
            Q0=makeQuery(id+"F55.opExtrude","CAP_FACE",FACE,{"disambiguationData":[OSD([sQuery(id+"F54.wireOp",EDGE,"E78"),sQuery(id+"F54.wireOp",EDGE,"E79"),sQuery(id+"F54.wireOp",EDGE,"E80"),sQuery(id+"F54.wireOp",EDGE,"E81"),sQuery(id+"F54.wireOp",EDGE,"E82"),sQuery(id+"F54.wireOp",EDGE,"E83")])],"isStart":true});
            var sketch = newSketch(context, id + "F58", { "sketchPlane" : qUnion([Q0])});
            skLineSegment(sketch, "E85.0", {"start": v(-7251.7, 1526.97) * mm, "end": v(-7251.7, 38.1) * mm});
            skLineSegment(sketch, "E85.1", {"start": v(-6870.7, 1629.06) * mm, "end": v(-7251.7, 1526.97) * mm});
            skLineSegment(sketch, "E85.2", {"start": v(-6870.7, 38.1) * mm, "end": v(-6870.7, 1629.06) * mm});
            skLineSegment(sketch, "E85.3", {"start": v(-7251.7, 38.1) * mm, "end": v(-6870.7, 38.1) * mm});
            skSolve(sketch);
        }
        {
            var Q0;
            Q0 = qSketchRegion(id + "F58", true);
            extrude(context, id + "F59", {"entities" : qUnion([Q0]), "operationType" : NewBodyOperationType.REMOVE, "oppositeDirection" : true, "depth" : 12.7 * mm});
        }
        {
            var Q0;
            Q0=makeQuery(id+"F55.opExtrude","CAP_FACE",FACE,{"disambiguationData":[OSD([sQuery(id+"F54.wireOp",EDGE,"E78"),sQuery(id+"F54.wireOp",EDGE,"E79"),sQuery(id+"F54.wireOp",EDGE,"E80"),sQuery(id+"F54.wireOp",EDGE,"E81"),sQuery(id+"F54.wireOp",EDGE,"E82"),sQuery(id+"F54.wireOp",EDGE,"E83")])],"isStart":false});
            var sketch = newSketch(context, id + "F60", { "sketchPlane" : qUnion([Q0])});
            skLineSegment(sketch, "E86.0", {"start": v(7251.7, 38.1) * mm, "end": v(7251.7, 1526.97) * mm});
            skLineSegment(sketch, "E86.1", {"start": v(6870.7, 38.1) * mm, "end": v(7251.7, 38.1) * mm});
            skLineSegment(sketch, "E86.2", {"start": v(6870.7, 1629.06) * mm, "end": v(6870.7, 38.1) * mm});
            skLineSegment(sketch, "E86.3", {"start": v(7251.7, 1526.97) * mm, "end": v(6870.7, 1629.06) * mm});
            skSolve(sketch);
        }
        {
            var Q0;
            Q0 = qSketchRegion(id + "F60", true);
            extrude(context, id + "F61", {"entities" : qUnion([Q0]), "operationType" : NewBodyOperationType.REMOVE, "oppositeDirection" : true, "depth" : 12.7 * mm});
        }
        {
            var Q0;
            Q0=makeQuery(id+"F55.opExtrude","SWEPT_FACE",FACE,{"disambiguationData":[OSD([sQuery(id+"F54.wireOp",EDGE,"E79")])]});
            var sketch = newSketch(context, id + "F62", { "sketchPlane" : qUnion([Q0])});
            skLineSegment(sketch, "E87.0", {"start": v(3556, 6677.63) * mm, "end": v(3556, 6152.6) * mm});
            skLineSegment(sketch, "E87.1", {"start": v(4724.4, 6677.63) * mm, "end": v(3556, 6677.63) * mm});
            skLineSegment(sketch, "E87.2", {"start": v(4724.4, 6152.6) * mm, "end": v(4724.4, 6677.63) * mm});
            skLineSegment(sketch, "E87.3", {"start": v(3556, 6152.6) * mm, "end": v(4724.4, 6152.6) * mm});
            skSolve(sketch);
        }
        {
            var Q0;
            Q0 = qSketchRegion(id + "F62", true);
            extrude(context, id + "F63", {"entities" : qUnion([Q0]), "operationType" : NewBodyOperationType.ADD, "depth" : 12.7 * mm});
        }
        {
            var Q0;
            Q0=makeQuery(id+"F9.boolean.opBoolean","COPY",FACE,{"derivedFrom":makeQuery(id+"F9.opExtrude","CAP_FACE",FACE,{"disambiguationData":[OSD([sQuery(id+"F0.wireOp",EDGE,"E4"),sQuery(id+"F2.wireOp",EDGE,"E6.bottom"),sQuery(id+"F2.wireOp",EDGE,"E6.top"),sQuery(id+"F2.wireOp",EDGE,"E6.right"),sQuery(id+"F8.wireOp",EDGE,"E13.right"),sQuery(id+"F8.wireOp",EDGE,"E14.right")])],"isStart":false})});
            var sketch = newSketch(context, id + "F64", { "sketchPlane" : qUnion([Q0])});
            skLineSegment(sketch, "E88.bottom", {"start": v(-3886.2, 2705.1) * mm, "end": v(-1752.6, 2705.1) * mm});
            skLineSegment(sketch, "E88.top", {"start": v(-3886.2, 2374.9) * mm, "end": v(-1752.6, 2374.9) * mm});
            skLineSegment(sketch, "E88.left", {"start": v(-3886.2, 2705.1) * mm, "end": v(-3886.2, 2374.9) * mm});
            skLineSegment(sketch, "E88.right", {"start": v(-1752.6, 2705.1) * mm, "end": v(-1752.6, 2374.9) * mm});
            skLineSegment(sketch, "E89.bottom", {"start": v(-5994.4, 2509.35) * mm, "end": v(-5080, 2509.35) * mm});
            skLineSegment(sketch, "E89.top", {"start": v(-5994.4, 1747.35) * mm, "end": v(-5080, 1747.35) * mm});
            skLineSegment(sketch, "E89.left", {"start": v(-5994.4, 2509.35) * mm, "end": v(-5994.4, 1747.35) * mm});
            skLineSegment(sketch, "E89.right", {"start": v(-5080, 2509.35) * mm, "end": v(-5080, 1747.35) * mm});
            skSolve(sketch);
        }
        {
            var Q0;
            Q0 = qSketchRegion(id + "F64", true);
            extrude(context, id + "F65", {"entities" : qUnion([Q0]), "operationType" : NewBodyOperationType.ADD, "depth" : 25.4 * mm});
        }
        {
            var Q0;
            Q0=makeQuery(id+"F18.boolean.opBoolean","MERGE",FACE,{"derivedFrom":[makeQuery(id+"F13.opExtrude","SWEPT_FACE",FACE,{"disambiguationData":[OSD([sQuery(id+"F12.wireOp",EDGE,"E16.bottom")])]}),makeQuery(id+"F13.opExtrude","SWEPT_FACE",FACE,{"disambiguationData":[OSD([sQuery(id+"F12.wireOp",EDGE,"E23.bottom")])]}),makeQuery(id+"F18.opExtrude","SWEPT_FACE",FACE,{"disambiguationData":[OSD([sQuery(id+"F17.wireOp",EDGE,"E37.bottom")])]})]});
            var sketch = newSketch(context, id + "F66", { "sketchPlane" : qUnion([Q0])});
            skLineSegment(sketch, "E90.bottom", {"start": v(152.4, 0) * mm, "end": v(4978.4, 0) * mm});
            skLineSegment(sketch, "E90.top", {"start": v(152.4, -254) * mm, "end": v(4978.4, -254) * mm});
            skLineSegment(sketch, "E90.left", {"start": v(152.4, 0) * mm, "end": v(152.4, -254) * mm});
            skLineSegment(sketch, "E90.right", {"start": v(4978.4, 0) * mm, "end": v(4978.4, -254) * mm});
            skSolve(sketch);
        }
        {
            var Q0;
            Q0 = qSketchRegion(id + "F66", true);
            extrude(context, id + "F67", {"entities" : qUnion([Q0]), "operationType" : NewBodyOperationType.ADD, "depth" : 12.7 * mm});
        }
    });
